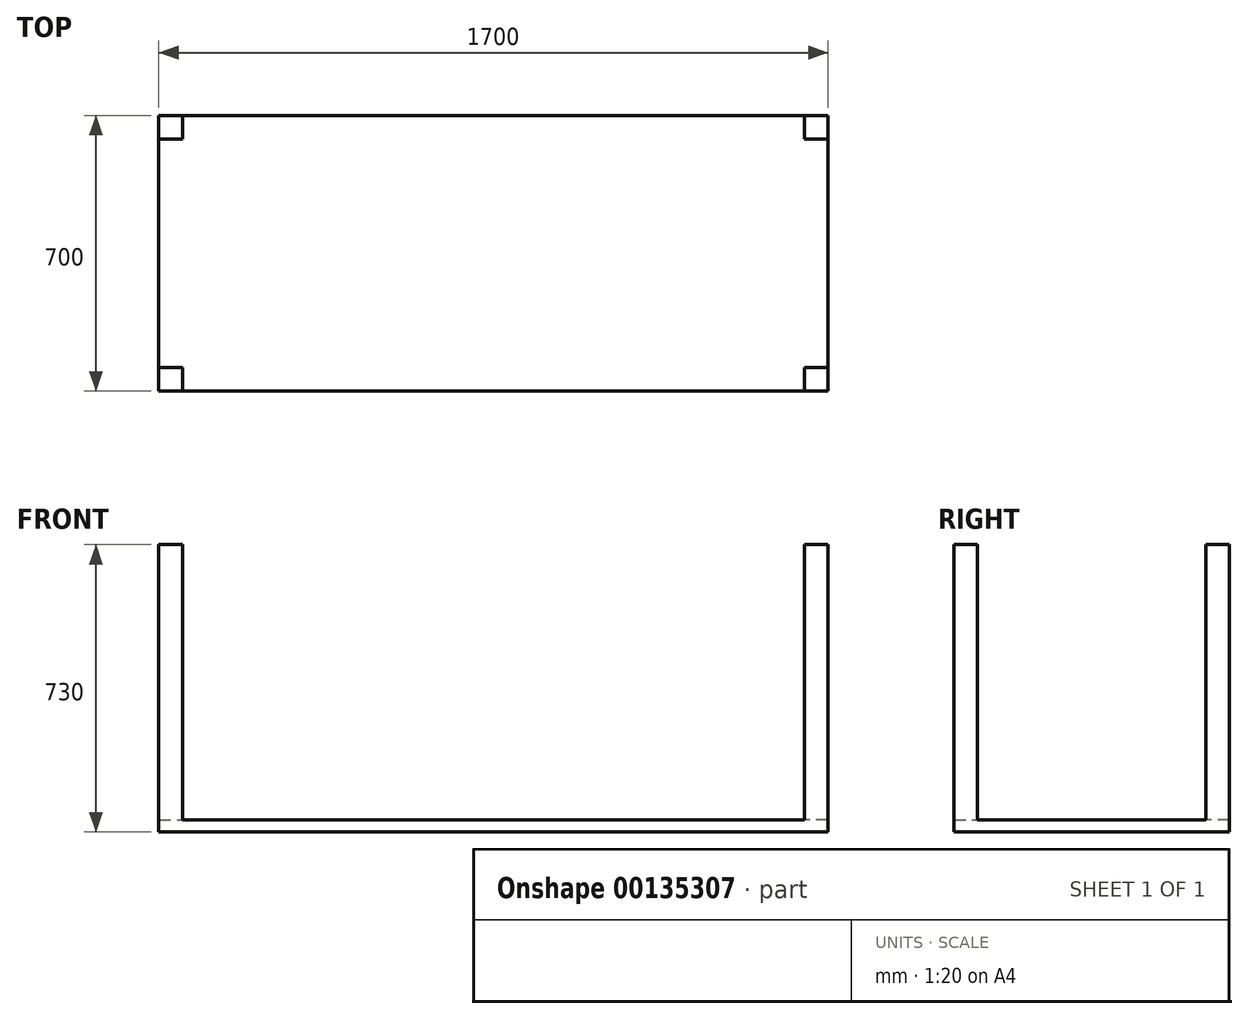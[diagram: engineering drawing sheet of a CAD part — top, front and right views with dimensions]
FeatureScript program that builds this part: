
annotation { "Feature Type Name" : "Feature", "Feature Type Description" : "" }
export const myFeature = defineFeature(function(context is Context, id is Id, definition is map)
    precondition{}
    {
        {
            var Q0;
            Q0=qCreatedBy(makeId("Top.planeOp"),FACE);
            var sketch = newSketch(context, id + "F0", { "sketchPlane" : qUnion([Q0])});
            skLineSegment(sketch, "E0.bottom", {"start": v(-850, -350) * mm, "end": v(850, -350) * mm});
            skLineSegment(sketch, "E0.top", {"start": v(-850, 350) * mm, "end": v(850, 350) * mm});
            skLineSegment(sketch, "E0.left", {"start": v(-850, -350) * mm, "end": v(-850, 350) * mm});
            skLineSegment(sketch, "E0.right", {"start": v(850, -350) * mm, "end": v(850, 350) * mm});
            skPoint(sketch, "E0.middle", {"position": v(0, 0) * mm});
            skSolve(sketch);
        }
        {
            var Q0;
            Q0=makeQuery(id+"F0.imprint","IMPRINT",FACE,{"disambiguationData":[TD([[makeQuery(id+"F0.imprint","IMPRINT",EDGE,{"derivedFrom":sQuery(id+"F0.wireOp",EDGE,"E0.bottom")}),1.0]])]});
            extrude(context, id + "F1", {"entities" : qUnion([Q0]), "depth" : 30 * mm});
        }
        {
            var Q0;
            Q0=makeQuery(id+"F1.opExtrude","CAP_FACE",FACE,{"disambiguationData":[OSD([sQuery(id+"F0.wireOp",EDGE,"E0.bottom"),sQuery(id+"F0.wireOp",EDGE,"E0.top"),sQuery(id+"F0.wireOp",EDGE,"E0.left"),sQuery(id+"F0.wireOp",EDGE,"E0.right")])],"isStart":false});
            var sketch = newSketch(context, id + "F2", { "sketchPlane" : qUnion([Q0])});
            skLineSegment(sketch, "E1.bottom", {"start": v(-850, 350) * mm, "end": v(-790, 350) * mm});
            skLineSegment(sketch, "E1.top", {"start": v(-850, 290) * mm, "end": v(-790, 290) * mm});
            skLineSegment(sketch, "E1.left", {"start": v(-850, 350) * mm, "end": v(-850, 290) * mm});
            skLineSegment(sketch, "E1.right", {"start": v(-790, 350) * mm, "end": v(-790, 290) * mm});
            skLineSegment(sketch, "E2.bottom", {"start": v(-850, -350) * mm, "end": v(-790, -350) * mm});
            skLineSegment(sketch, "E2.top", {"start": v(-850, -290) * mm, "end": v(-790, -290) * mm});
            skLineSegment(sketch, "E2.left", {"start": v(-850, -350) * mm, "end": v(-850, -290) * mm});
            skLineSegment(sketch, "E2.right", {"start": v(-790, -350) * mm, "end": v(-790, -290) * mm});
            skLineSegment(sketch, "E3.bottom", {"start": v(850, 350) * mm, "end": v(790, 350) * mm});
            skLineSegment(sketch, "E3.top", {"start": v(850, 290) * mm, "end": v(790, 290) * mm});
            skLineSegment(sketch, "E3.left", {"start": v(850, 350) * mm, "end": v(850, 290) * mm});
            skLineSegment(sketch, "E3.right", {"start": v(790, 350) * mm, "end": v(790, 290) * mm});
            skLineSegment(sketch, "E4.bottom", {"start": v(850, -350) * mm, "end": v(790, -350) * mm});
            skLineSegment(sketch, "E4.top", {"start": v(850, -290) * mm, "end": v(790, -290) * mm});
            skLineSegment(sketch, "E4.left", {"start": v(850, -350) * mm, "end": v(850, -290) * mm});
            skLineSegment(sketch, "E4.right", {"start": v(790, -350) * mm, "end": v(790, -290) * mm});
            skSolve(sketch);
        }
        {
            var Q0;
            Q0 = qSketchRegion(id + "F2", true);
            extrude(context, id + "F3", {"entities" : qUnion([Q0]), "operationType" : NewBodyOperationType.ADD, "depth" : 700 * mm});
        }
    });
